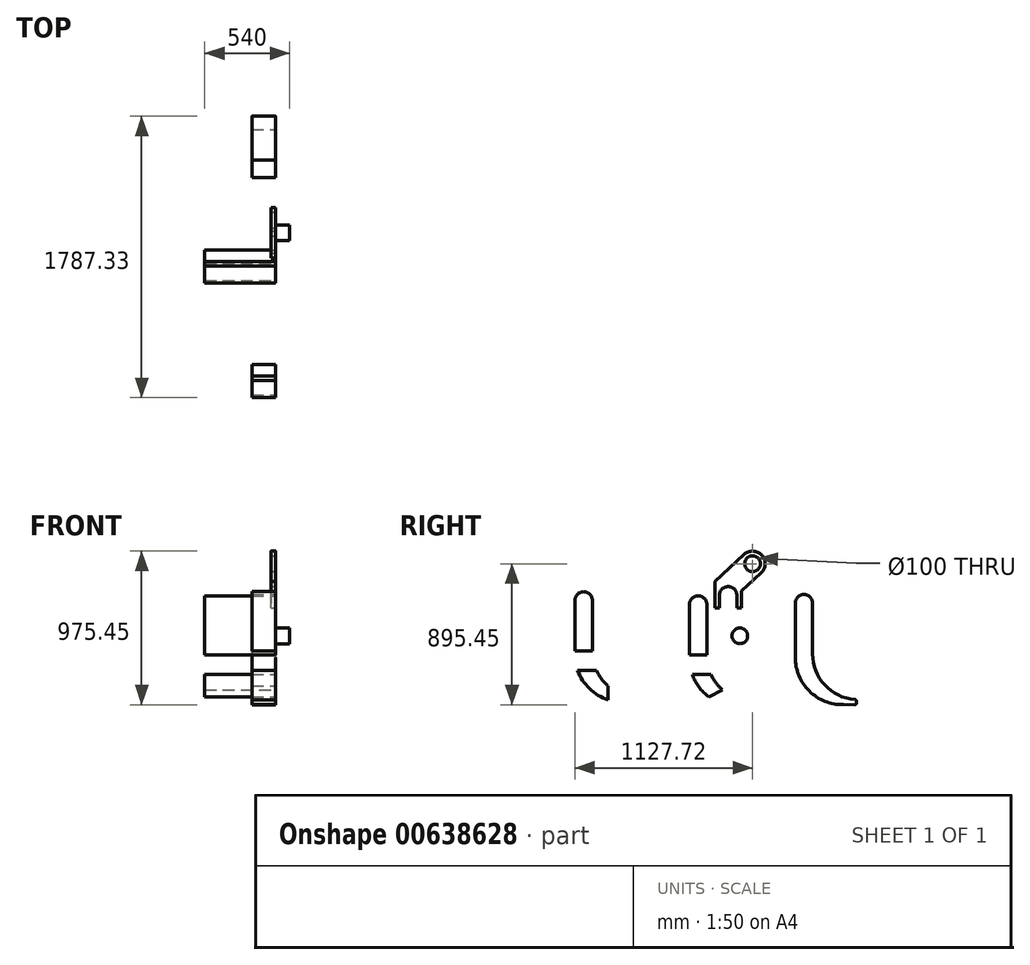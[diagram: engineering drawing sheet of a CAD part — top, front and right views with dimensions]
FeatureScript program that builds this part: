
annotation { "Feature Type Name" : "Feature", "Feature Type Description" : "" }
export const myFeature = defineFeature(function(context is Context, id is Id, definition is map)
    precondition{}
    {
        {
            var Q0;
            Q0=qCreatedBy(makeId("Right.planeOp"),FACE);
            var sketch = newSketch(context, id + "F0", { "sketchPlane" : qUnion([Q0])});
            skLineSegment(sketch, "E0", {"start": v(0, 0) * mm, "end": v(0, 295) * mm});
            skLineSegment(sketch, "E1", {"start": v(55, 350) * mm, "end": v(55, 350) * mm});
            skLineSegment(sketch, "E2", {"start": v(110, 295) * mm, "end": v(110, 0) * mm});
            skLineSegment(sketch, "E3", {"start": v(0, 0) * mm, "end": v(0, -50) * mm});
            skLineSegment(sketch, "E4", {"start": v(110, -50) * mm, "end": v(110, 0) * mm});
            skArc(sketch, "E5.filletArc", {"start": v(0, -50) * mm, "mid": v(89.52, -263.78) * mm, "end": v(304.65, -350) * mm});
            skLineSegment(sketch, "E6", {"start": v(110, -26.66) * mm, "end": v(110, -50) * mm});
            skArc(sketch, "E7.filletArc", {"start": v(110, -26.66) * mm, "mid": v(187.67, -225.1) * mm, "end": v(379.4, -318.07) * mm});
            skLineSegment(sketch, "E8", {"start": v(378.59, -350.27) * mm, "end": v(304.65, -350) * mm});
            skArc(sketch, "E9.filletArc", {"start": v(55, 350) * mm, "mid": v(16.1, 333.9) * mm, "end": v(0, 295) * mm});
            skArc(sketch, "E10.filletArc", {"start": v(110, 295) * mm, "mid": v(93.9, 333.9) * mm, "end": v(55, 350) * mm});
            skLineSegment(sketch, "E11", {"start": v(0, 295) * mm, "end": v(110, 295) * mm, "construction": true});
            skLineSegment(sketch, "E12", {"start": v(55, 350) * mm, "end": v(55, -350) * mm, "construction": true});
            skLineSegment(sketch, "E13", {"start": v(388.63, -328.04) * mm, "end": v(388.63, -340.27) * mm});
            skPoint(sketch, "E14.visualSharp", {"position": v(388.63, -350.31) * mm});
            skArc(sketch, "E14.filletArc", {"start": v(378.59, -350.27) * mm, "mid": v(385.68, -347.36) * mm, "end": v(388.63, -340.27) * mm});
            skPoint(sketch, "E15.visualSharp", {"position": v(388.63, -318.65) * mm});
            skArc(sketch, "E15.filletArc", {"start": v(388.63, -328.04) * mm, "mid": v(385.97, -321.25) * mm, "end": v(379.4, -318.07) * mm});
            skSolve(sketch);
        }
        {
            var Q0;
            Q0=makeQuery(id+"F0.imprint","IMPRINT",FACE,{"disambiguationData":[TD([[makeQuery(id+"F0.imprint","IMPRINT",EDGE,{"derivedFrom":sQuery(id+"F0.wireOp",EDGE,"E0")}),-1.0]])]});
            extrude(context, id + "F1", {"entities" : qUnion([Q0]), "oppositeDirection" : true, "depth" : 150 * mm, "offsetDistance" : 25 * mm});
        }
        {
            var Q0;
            Q0=qCreatedBy(makeId("Right.planeOp"),FACE);
            var sketch = newSketch(context, id + "F2", { "sketchPlane" : qUnion([Q0])});
            skLineSegment(sketch, "E16", {"start": v(-671.48, 54.5) * mm, "end": v(-671.48, 286.6) * mm});
            skLineSegment(sketch, "E17", {"start": v(-616.48, 341.6) * mm, "end": v(-616.48, 341.6) * mm});
            skLineSegment(sketch, "E18", {"start": v(-561.48, 286.6) * mm, "end": v(-561.48, 54.5) * mm});
            skLineSegment(sketch, "E19", {"start": v(-671.48, 54.5) * mm, "end": v(-671.48, -34.45) * mm});
            skLineSegment(sketch, "E20", {"start": v(-561.48, 4.5) * mm, "end": v(-561.48, 54.5) * mm});
            skArc(sketch, "E21.filletArc", {"start": v(-654.45, -158.05) * mm, "mid": v(-611.66, -238.17) * mm, "end": v(-546.86, -301.82) * mm});
            skLineSegment(sketch, "E22", {"start": v(-561.48, 4.5) * mm, "end": v(-561.48, -34.45) * mm});
            skArc(sketch, "E23.filletArc", {"start": v(-534.84, -158.05) * mm, "mid": v(-503.38, -211.89) * mm, "end": v(-461.48, -258.05) * mm});
            skArc(sketch, "E24.filletArc", {"start": v(-616.48, 341.6) * mm, "mid": v(-655.37, 325.49) * mm, "end": v(-671.48, 286.6) * mm});
            skArc(sketch, "E25.filletArc", {"start": v(-561.48, 286.6) * mm, "mid": v(-577.6, 325.49) * mm, "end": v(-616.48, 341.6) * mm});
            skLineSegment(sketch, "E26", {"start": v(-671.48, 286.6) * mm, "end": v(-561.48, 286.6) * mm, "construction": true});
            skLineSegment(sketch, "E27", {"start": v(-616.48, 341.6) * mm, "end": v(-616.48, -358.4) * mm, "construction": true});
            skLineSegment(sketch, "E28", {"start": v(-561.48, -34.45) * mm, "end": v(-671.48, -34.45) * mm});
            skLineSegment(sketch, "E29", {"start": v(-534.84, -158.05) * mm, "end": v(-654.45, -158.05) * mm});
            skLineSegment(sketch, "E30", {"start": v(-461.48, -258.05) * mm, "end": v(-546.86, -301.82) * mm});
            skSolve(sketch);
        }
        {
            var Q0;
            Q0 = qSketchRegion(id + "F2", true);
            extrude(context, id + "F3", {"entities" : qUnion([Q0]), "oppositeDirection" : true, "depth" : 450 * mm, "offsetDistance" : 25 * mm});
        }
        {
            var Q0;
            Q0=qCreatedBy(makeId("Right.planeOp"),FACE);
            var sketch = newSketch(context, id + "F4", { "sketchPlane" : qUnion([Q0])});
            skLineSegment(sketch, "E31", {"start": v(-1398.7, 80.39) * mm, "end": v(-1398.7, 312.5) * mm});
            skLineSegment(sketch, "E32", {"start": v(-1343.7, 367.5) * mm, "end": v(-1343.7, 367.5) * mm});
            skLineSegment(sketch, "E33", {"start": v(-1288.7, 312.5) * mm, "end": v(-1288.7, 80.39) * mm});
            skLineSegment(sketch, "E34", {"start": v(-1398.7, 80.39) * mm, "end": v(-1398.7, -8.55) * mm});
            skLineSegment(sketch, "E35", {"start": v(-1288.7, 30.39) * mm, "end": v(-1288.7, 80.39) * mm});
            skArc(sketch, "E36.filletArc", {"start": v(-1381.67, -132.16) * mm, "mid": v(-1307.2, -248.22) * mm, "end": v(-1188.7, -318.72) * mm});
            skLineSegment(sketch, "E37", {"start": v(-1288.7, 30.39) * mm, "end": v(-1288.7, -8.55) * mm});
            skArc(sketch, "E38.filletArc", {"start": v(-1262.05, -132.16) * mm, "mid": v(-1230.6, -186) * mm, "end": v(-1188.7, -232.16) * mm});
            skArc(sketch, "E39.filletArc", {"start": v(-1343.7, 367.5) * mm, "mid": v(-1382.6, 351.38) * mm, "end": v(-1398.7, 312.5) * mm});
            skArc(sketch, "E40.filletArc", {"start": v(-1288.7, 312.5) * mm, "mid": v(-1304.81, 351.38) * mm, "end": v(-1343.7, 367.5) * mm});
            skLineSegment(sketch, "E41", {"start": v(-1398.7, 312.5) * mm, "end": v(-1288.7, 312.5) * mm, "construction": true});
            skLineSegment(sketch, "E42", {"start": v(-1343.7, 367.5) * mm, "end": v(-1343.7, -332.5) * mm, "construction": true});
            skLineSegment(sketch, "E43", {"start": v(-1288.7, -8.55) * mm, "end": v(-1398.7, -8.55) * mm});
            skLineSegment(sketch, "E44", {"start": v(-1262.05, -132.16) * mm, "end": v(-1381.67, -132.16) * mm});
            skLineSegment(sketch, "E45", {"start": v(-1188.7, -232.16) * mm, "end": v(-1188.7, -318.72) * mm});
            skLineSegment(sketch, "E46.trimOffspring", {"start": v(-1188.7, -232.16) * mm, "end": v(-1188.7, -318.72) * mm, "construction": true});
            skSolve(sketch);
        }
        {
            var Q0;
            Q0 = qSketchRegion(id + "F4", true);
            extrude(context, id + "F5", {"entities" : qUnion([Q0]), "oppositeDirection" : true, "depth" : 150 * mm, "offsetDistance" : 25 * mm});
        }
        {
            var Q0;
            Q0=qCreatedBy(makeId("Right.planeOp"),FACE);
            var sketch = newSketch(context, id + "F6", { "sketchPlane" : qUnion([Q0])});
            skLineSegment(sketch, "E47", {"start": v(-480.98, 265.18) * mm, "end": v(-480.98, 345.18) * mm});
            skLineSegment(sketch, "E48", {"start": v(-425.98, 400.18) * mm, "end": v(-425.98, 400.18) * mm});
            skLineSegment(sketch, "E49", {"start": v(-370.98, 345.18) * mm, "end": v(-370.98, 265.18) * mm});
            skLineSegment(sketch, "E50", {"start": v(-480.98, 50.18) * mm, "end": v(-480.98, 0.18) * mm});
            skLineSegment(sketch, "E51", {"start": v(-370.98, 0.18) * mm, "end": v(-370.98, 50.18) * mm});
            skArc(sketch, "E52.filletArc", {"start": v(-480.98, 0.18) * mm, "mid": v(-391.46, -213.6) * mm, "end": v(-176.33, -299.82) * mm});
            skLineSegment(sketch, "E53", {"start": v(-370.98, 24.13) * mm, "end": v(-370.98, 0.18) * mm});
            skArc(sketch, "E54.filletArc", {"start": v(-370.98, 24.13) * mm, "mid": v(-291.27, -179.52) * mm, "end": v(-94.48, -274.94) * mm});
            skLineSegment(sketch, "E55", {"start": v(-95.3, -300.12) * mm, "end": v(-176.33, -299.82) * mm});
            skArc(sketch, "E56.filletArc", {"start": v(-425.98, 400.18) * mm, "mid": v(-464.87, 384.07) * mm, "end": v(-480.98, 345.18) * mm});
            skArc(sketch, "E57.filletArc", {"start": v(-370.98, 345.18) * mm, "mid": v(-387.09, 384.07) * mm, "end": v(-425.98, 400.18) * mm});
            skLineSegment(sketch, "E58", {"start": v(-480.98, 345.18) * mm, "end": v(-370.98, 345.18) * mm, "construction": true});
            skLineSegment(sketch, "E59", {"start": v(-425.98, 400.18) * mm, "end": v(-425.98, -299.82) * mm, "construction": true});
            skLineSegment(sketch, "E60", {"start": v(-85.27, -284.91) * mm, "end": v(-85.27, -290.12) * mm});
            skPoint(sketch, "E61.visualSharp", {"position": v(-85.27, -300.16) * mm});
            skArc(sketch, "E61.filletArc", {"start": v(-95.3, -300.12) * mm, "mid": v(-88.2, -297.2) * mm, "end": v(-85.27, -290.12) * mm});
            skPoint(sketch, "E62.visualSharp", {"position": v(-85.27, -275.53) * mm});
            skArc(sketch, "E62.filletArc", {"start": v(-85.27, -284.91) * mm, "mid": v(-87.92, -278.12) * mm, "end": v(-94.48, -274.94) * mm});
            skLineSegment(sketch, "E63", {"start": v(-370.98, 345.18) * mm, "end": v(-270.98, 345.18) * mm, "construction": true});
            skLineSegment(sketch, "E64", {"start": v(-270.98, 345.18) * mm, "end": v(-270.98, 545.18) * mm, "construction": true});
            skCircle(sketch, "E65", {"center": v(-270.98, 545.18) * mm, "radius": 50 * mm});
            skLineSegment(sketch, "E66", {"start": v(-480.98, 345.18) * mm, "end": v(-480.98, 332.04) * mm});
            skLineSegment(sketch, "E67", {"start": v(-510.98, 432.04) * mm, "end": v(-325.32, 603.89) * mm});
            skLineSegment(sketch, "E68", {"start": v(-212.27, 599.52) * mm, "end": v(-212.27, 599.52) * mm});
            skLineSegment(sketch, "E69", {"start": v(-216.64, 486.47) * mm, "end": v(-340.98, 371.38) * mm});
            skPoint(sketch, "E70.visualSharp", {"position": v(-266.61, 658.23) * mm});
            skArc(sketch, "E70.filletArc", {"start": v(-212.27, 599.52) * mm, "mid": v(-267.9, 625.12) * mm, "end": v(-325.32, 603.89) * mm});
            skPoint(sketch, "E71.visualSharp", {"position": v(-157.93, 540.81) * mm});
            skArc(sketch, "E71.filletArc", {"start": v(-216.64, 486.47) * mm, "mid": v(-191.04, 542.1) * mm, "end": v(-212.27, 599.52) * mm});
            skLineSegment(sketch, "E72", {"start": v(-510.98, 432.04) * mm, "end": v(-510.98, 265.18) * mm});
            skLineSegment(sketch, "E73", {"start": v(-510.98, 265.18) * mm, "end": v(-480.98, 265.18) * mm});
            skLineSegment(sketch, "E74", {"start": v(-340.98, 371.38) * mm, "end": v(-340.98, 265.18) * mm});
            skLineSegment(sketch, "E75.trimOffspring", {"start": v(-370.98, 265.18) * mm, "end": v(-340.98, 265.18) * mm});
            skSolve(sketch);
        }
        {
            var Q0;
            Q0 = qSketchRegion(id + "F6", true);
            extrude(context, id + "F7", {"entities" : qUnion([Q0]), "oppositeDirection" : true, "depth" : 30 * mm, "offsetDistance" : 25 * mm});
        }
        {
            var Q0;
            Q0=qCreatedBy(makeId("Right.planeOp"),FACE);
            var sketch = newSketch(context, id + "F8", { "sketchPlane" : qUnion([Q0])});
            skCircle(sketch, "E76", {"center": v(-352.12, 86.9) * mm, "radius": 50 * mm});
            skSolve(sketch);
        }
        {
            var Q0;
            Q0 = qSketchRegion(id + "F8", true);
            extrude(context, id + "F9", {"entities" : qUnion([Q0]), "depth" : 90 * mm, "offsetDistance" : 25 * mm});
        }
    });
